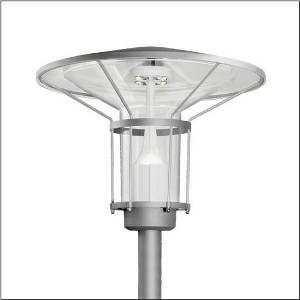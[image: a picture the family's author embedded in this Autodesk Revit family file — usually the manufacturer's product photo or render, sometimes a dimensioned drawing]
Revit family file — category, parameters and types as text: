
# Revit family: laterne_classic_iq___st1_2a_5xa5245mf14h_178e
name_source: partatom
category: Lighting Fixtures
units: mm (PartAtom-declared; Revit-internal decimal feet)

## family parameters
Cut with Voids When Loaded = No
Host = Face
Light Source = No
Part Type = Normal
Room Calculation Point = No
Round Connector Dimension = Use Diameter
Shared = No

## types (1)
- --- (1 x LED, 1380 lm, 11.8 W, 2700K)
    Apparent Load = 12 VA
    CIE Flux Codes = 21 60 93 97 100
    Color Rendering = 70
    Color Temperature = 2700K
    Default Elevation = 1800 mm
    Description = Lantern Classic iQ, mast luminaire, Module 540 iQ-SR, primary light control with 3 zone facetted reflector, of plastic, silver coated, highly specular, structured, primary optical cover: cover, of PMMA, transparent, light distribution: ST1.2a, light emission: direct distribution, primary light characteristic: asymmetric, installation type: post-top, LED, High Power LED, rated luminous flux: 1.380lm, luminous efficacy: 117lm/W, light colour: 727, colour temperature: 2700K, control gear: ECG iQ, control: presetting dimming logarithmic, Street-Remote, Auto-Match, Temp-Guard, Lumen-Switch, Night-Set, Smart-Wire, Light-Fading, Desk-Remote (wireless, voltage-free reading and setting of iQ features in the workshop via application-optimized NFC function/RFID function), optimised constant luminous flux control (CLO 2.0), with terminal, 6-pole, max. 2.5mm², mains connection: 220..240V, AC, 50/60Hz, start of lifetime: 12W, end of lifetime: 12W, reduction: 6W, luminaire housing, upper part, of glass-fibre reinforced polyester, coated, Siteco® metallic grey (DB 702S), diameter: 750mm, height: 596mm, spigot size: d x l = 76 x 70mm (post-top) | with reducer (optional accessory) 60 x 70mm, post-top mast mounting element, of diecast aluminium, coated, Siteco® metallic grey (DB 702S), Module 540 iQ-SR, traffic white (RAL 9016), equipment: standard, protection rating (complete): IP65, insulation class (complete): insulation class II (safety insulation), certification: CE, ENEC, VDE, packaging unit: 1 piece

Light Distribution: ST1.2a
    Height = 596 mm
    Lamp = 1 x LED
    Lamp Light Flux = 1380 lm
    Lamp Power = 11.8 W
    Lamp count = 1
    Length = 750 mm
    Luminous efficacy = 117 lm/W
    Manufacturer = Siteco
    ModVariant = No
    Model = 5XA5245MF14H
    Number of Poles = 1
    OnlyDefault = Yes
    Power Factor = 1
    Product Name = Laterne Classic iQ | ST1.2a
    Product group = mast luminaire | pylon top
    ProductGroupID = 6100
    Protection Class = Protection class II
    Protection Degree = IP 65
    RLX_Detail_Level = 1
    RlxData = <blob elided: 91681 chars, md5=d4cb9bb5>
    Socket = socket
    Standby Power = 0 W
    System Light Flux = 1380 lm
    System Power = 12 W
    Type Comments = factory setting: luminous flux: 100 % | dim-lin: 254 | 472 mA
    Type Image = l_1006052.jpg
    URL = http://relux.com
    VarID = @adj_063185
    Voltage = 0 V
    Weight = 0.00 kg
    Width = 0 mm  [stored 0 ft]

note: [stored X ft] marks values corroborated as IEEE doubles in the binary element streams (Revit-internal decimal feet)

## geometry (parser evidence)
native form markers: Blend x4, Sweep x11
no freeform markers — native parametric forms only
